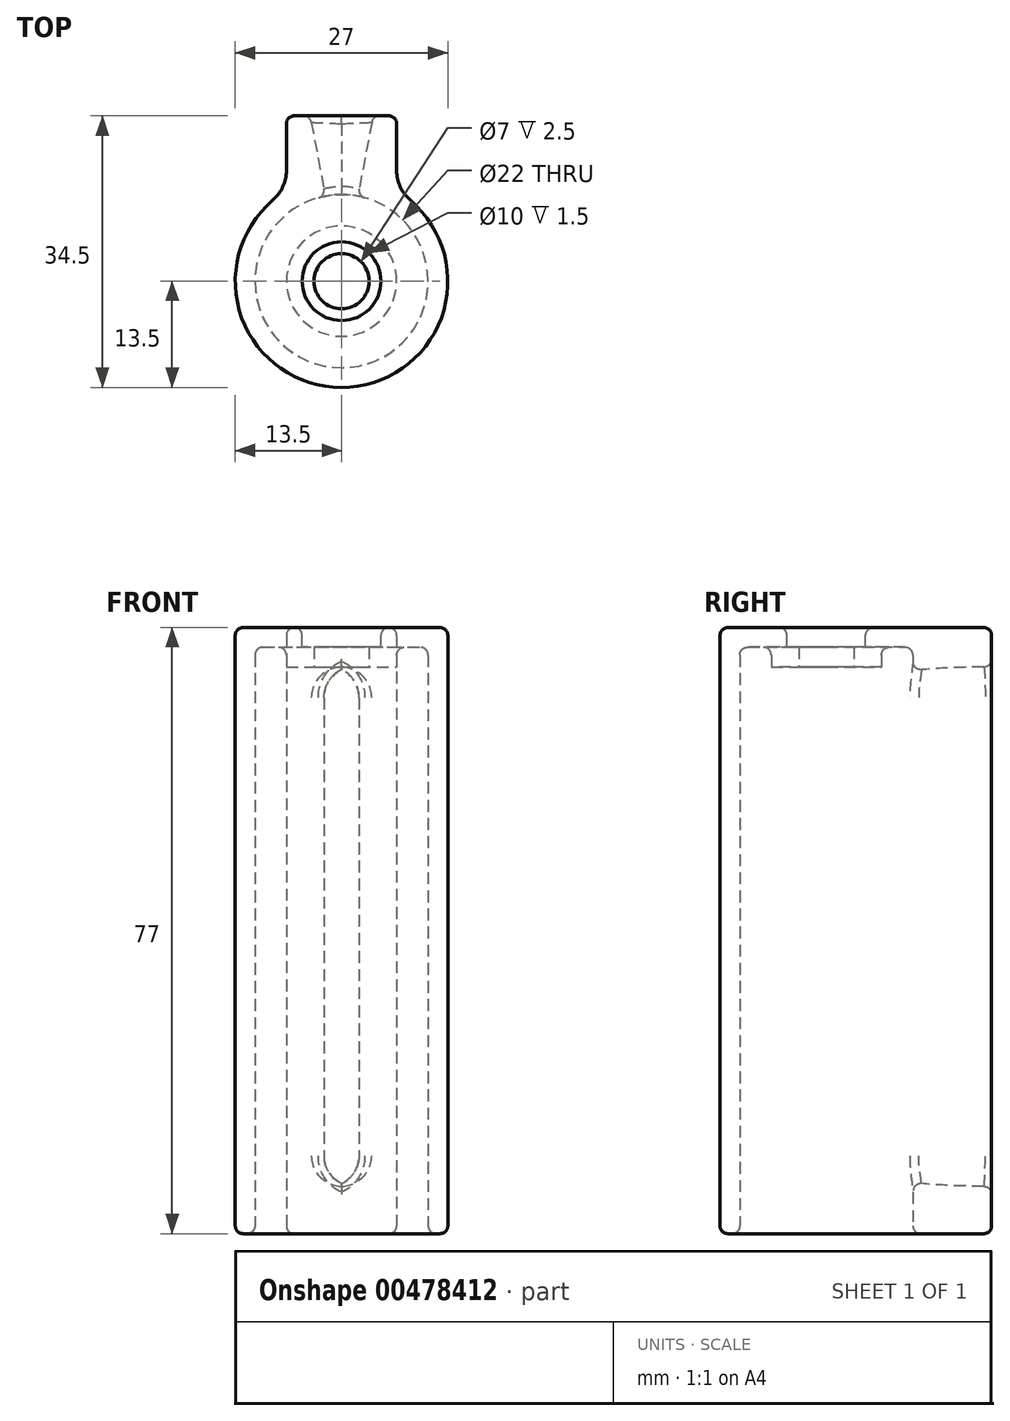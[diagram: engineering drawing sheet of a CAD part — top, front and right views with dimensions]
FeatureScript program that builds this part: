
annotation { "Feature Type Name" : "Feature", "Feature Type Description" : "" }
export const myFeature = defineFeature(function(context is Context, id is Id, definition is map)
    precondition{}
    {
        {
            var Q0;
            Q0=qCreatedBy(makeId("Top.planeOp"),FACE);
            var sketch = newSketch(context, id + "F0", { "sketchPlane" : qUnion([Q0])});
            skArc(sketch, "E0", {"start": v(-8.76, 10.27) * mm, "mid": v(0, -13.5) * mm, "end": v(8.76, 10.27) * mm});
            skCircle(sketch, "E1", {"center": v(0, 0) * mm, "radius": 3.5 * mm});
            skLineSegment(sketch, "E2", {"start": v(0, 0) * mm, "end": v(0, 21) * mm, "construction": true});
            skPoint(sketch, "E3.visualSharp", {"position": v(-7, 11.54) * mm});
            skArc(sketch, "E3.filletArc", {"start": v(-8.76, 10.27) * mm, "mid": v(-7.46, 11.98) * mm, "end": v(-7, 14.08) * mm});
            skPoint(sketch, "E4.visualSharp", {"position": v(7, 11.54) * mm});
            skArc(sketch, "E4.filletArc", {"start": v(7, 14.08) * mm, "mid": v(7.46, 11.98) * mm, "end": v(8.76, 10.27) * mm});
            skPoint(sketch, "E5.visualSharp", {"position": v(7, 21) * mm});
            skPoint(sketch, "E6.visualSharp", {"position": v(-7, 21) * mm});
            skLineSegment(sketch, "E7", {"start": v(-7, 14.08) * mm, "end": v(-7, 20) * mm});
            skLineSegment(sketch, "E8", {"start": v(-6, 21) * mm, "end": v(6, 21) * mm});
            skLineSegment(sketch, "E9", {"start": v(7, 20) * mm, "end": v(7, 14.08) * mm});
            skArc(sketch, "E10.filletArc", {"start": v(-6, 21) * mm, "mid": v(-6.7, 20.7) * mm, "end": v(-7, 20) * mm});
            skArc(sketch, "E11.filletArc", {"start": v(7, 20) * mm, "mid": v(6.7, 20.7) * mm, "end": v(6, 21) * mm});
            skSolve(sketch);
        }
        {
            var Q0;
            Q0 = qSketchRegion(id + "F0", true);
            extrude(context, id + "F1", {"entities" : qUnion([Q0]), "depth" : 77 * mm});
        }
        {
            var Q0;
            Q0=makeQuery(id+"F1.opExtrude","CAP_FACE",FACE,{"disambiguationData":[OSD([sQuery(id+"F0.wireOp",EDGE,"E0")])],"isStart":true});
            var sketch = newSketch(context, id + "F2", { "sketchPlane" : qUnion([Q0])});
            skCircle(sketch, "E12", {"center": v(0, 0) * mm, "radius": 11 * mm});
            skSolve(sketch);
        }
        {
            var Q0;
            Q0 = qSketchRegion(id + "F2", true);
            extrude(context, id + "F3", {"entities" : qUnion([Q0]), "operationType" : NewBodyOperationType.REMOVE, "oppositeDirection" : true, "depth" : 72 * mm});
        }
        {
            var Q0;
            Q0=makeQuery(id+"F3.boolean.opBoolean","COPY",FACE,{"derivedFrom":makeQuery(id+"F3.opExtrude","CAP_FACE",FACE,{"disambiguationData":[OSD([sQuery(id+"F2.wireOp",EDGE,"E12")])],"isStart":false})});
            var sketch = newSketch(context, id + "F4", { "sketchPlane" : qUnion([Q0])});
            skCircle(sketch, "E13", {"center": v(0, 0) * mm, "radius": 11 * mm});
            skCircle(sketch, "E14", {"center": v(0, 0) * mm, "radius": 7 * mm});
            skSolve(sketch);
        }
        {
            var Q0;
            Q0 = qSketchRegion(id + "F4", true);
            extrude(context, id + "F5", {"entities" : qUnion([Q0]), "operationType" : NewBodyOperationType.REMOVE, "oppositeDirection" : true, "depth" : 2.5 * mm});
        }
        {
            var Q0;
            Q0=qCreatedBy(makeId("Top.planeOp"),FACE);
            cPlane(context, id + "F6", {"entities" : qUnion([Q0]), "cplaneType" : CPlaneType.OFFSET, "offset" : 6 * mm, "width" : 150 * mm, "height" : 150 * mm});
        }
        {
            var Q0;
            Q0=qCreatedBy(id+"F6.planeOp",FACE);
            var sketch = newSketch(context, id + "F7", { "sketchPlane" : qUnion([Q0])});
            skLineSegment(sketch, "E15.0", {"start": v(-5, 21) * mm, "end": v(5, 21) * mm, "construction": true});
            skLineSegment(sketch, "E16", {"start": v(0, 21) * mm, "end": v(-4, 21) * mm});
            skLineSegment(sketch, "E17", {"start": v(-4, 21) * mm, "end": v(0, 0) * mm});
            skLineSegment(sketch, "E18", {"start": v(0, 21) * mm, "end": v(4, 21) * mm});
            skLineSegment(sketch, "E19", {"start": v(4, 21) * mm, "end": v(0, 0) * mm});
            skSolve(sketch);
        }
        {
            var Q0;
            Q0 = qSketchRegion(id + "F7", true);
            extrude(context, id + "F8", {"entities" : qUnion([Q0]), "operationType" : NewBodyOperationType.REMOVE, "oppositeDirection" : true, "depth" : -66 * mm});
        }
        {
            var Q0;
            Q0=makeQuery(id+"F1.opExtrude","CAP_FACE",FACE,{"disambiguationData":[OSD([sQuery(id+"F0.wireOp",EDGE,"E0"),sQuery(id+"F0.wireOp",EDGE,"E1"),sQuery(id+"F0.wireOp",EDGE,"E3.filletArc"),sQuery(id+"F0.wireOp",EDGE,"E4.filletArc"),sQuery(id+"F0.wireOp",EDGE,"E7"),sQuery(id+"F0.wireOp",EDGE,"E8"),sQuery(id+"F0.wireOp",EDGE,"E9"),sQuery(id+"F0.wireOp",EDGE,"E10.filletArc"),sQuery(id+"F0.wireOp",EDGE,"E11.filletArc")])],"isStart":false});
            var sketch = newSketch(context, id + "F9", { "sketchPlane" : qUnion([Q0])});
            skCircle(sketch, "E20", {"center": v(0, 0) * mm, "radius": 5 * mm});
            skSolve(sketch);
        }
        {
            var Q0;
            Q0 = qSketchRegion(id + "F9", true);
            extrude(context, id + "F10", {"entities" : qUnion([Q0]), "operationType" : NewBodyOperationType.REMOVE, "oppositeDirection" : true, "depth" : 2.5 * mm});
        }
        {
            var Q0;
            Q0=makeQuery(id+"F8.boolean.opBoolean","COPY",EDGE,{"derivedFrom":makeQuery(id+"F8.opExtrude","CAP_EDGE",EDGE,{"disambiguationData":[OSD([sQuery(id+"F7.wireOp",EDGE,"E17")])],"isStart":false})});
            var Q1;
            Q1=makeQuery(id+"F8.boolean.opBoolean","COPY",EDGE,{"derivedFrom":makeQuery(id+"F8.opExtrude","CAP_EDGE",EDGE,{"disambiguationData":[OSD([sQuery(id+"F7.wireOp",EDGE,"E19")])],"isStart":false})});
            var Q2;
            Q2=makeQuery(id+"F8.boolean.opBoolean","COPY",EDGE,{"derivedFrom":makeQuery(id+"F8.opExtrude","CAP_EDGE",EDGE,{"disambiguationData":[OSD([sQuery(id+"F7.wireOp",EDGE,"E19")])],"isStart":true})});
            var Q3;
            Q3=makeQuery(id+"F8.boolean.opBoolean","COPY",EDGE,{"derivedFrom":makeQuery(id+"F8.opExtrude","CAP_EDGE",EDGE,{"disambiguationData":[OSD([sQuery(id+"F7.wireOp",EDGE,"E17")])],"isStart":true})});
            fillet(context, id + "F11", {"entities" : qUnion([Q0, Q1, Q2, Q3]), "radius" : 3.9 * mm, "tangentPropagation" : true, "allowEdgeOverflow" : false});
        }
        {
            var Q0;
            Q0=makeQuery(id+"F1.opExtrude","CAP_FACE",FACE,{"disambiguationData":[OSD([sQuery(id+"F0.wireOp",EDGE,"E0"),sQuery(id+"F0.wireOp",EDGE,"E1"),sQuery(id+"F0.wireOp",EDGE,"E3.filletArc"),sQuery(id+"F0.wireOp",EDGE,"E4.filletArc"),sQuery(id+"F0.wireOp",EDGE,"E7"),sQuery(id+"F0.wireOp",EDGE,"E8"),sQuery(id+"F0.wireOp",EDGE,"E9"),sQuery(id+"F0.wireOp",EDGE,"E10.filletArc"),sQuery(id+"F0.wireOp",EDGE,"E11.filletArc")])],"isStart":false});
            var Q1;
            Q1=makeQuery(id+"F1.opExtrude","CAP_FACE",FACE,{"disambiguationData":[OSD([sQuery(id+"F0.wireOp",EDGE,"E0"),sQuery(id+"F0.wireOp",EDGE,"E1"),sQuery(id+"F0.wireOp",EDGE,"E3.filletArc"),sQuery(id+"F0.wireOp",EDGE,"E4.filletArc"),sQuery(id+"F0.wireOp",EDGE,"E7"),sQuery(id+"F0.wireOp",EDGE,"E8"),sQuery(id+"F0.wireOp",EDGE,"E9"),sQuery(id+"F0.wireOp",EDGE,"E10.filletArc"),sQuery(id+"F0.wireOp",EDGE,"E11.filletArc")])],"isStart":true});
            var Q2;
            Q2=makeQuery(id+"F1.opExtrude","SWEPT_FACE",FACE,{"disambiguationData":[OSD([sQuery(id+"F0.wireOp",EDGE,"E8")])]});
            var Q3;
            Q3=makeQuery(id+"F8.boolean.opBoolean","INTERSECT",EDGE,{"derivedFrom":[makeQuery(id+"F5.boolean.opBoolean","MERGE",FACE,{"derivedFrom":[makeQuery(id+"F3.boolean.opBoolean","COPY",FACE,{"derivedFrom":makeQuery(id+"F3.opExtrude","SWEPT_FACE",FACE,{"disambiguationData":[OSD([sQuery(id+"F2.wireOp",EDGE,"E12")])]})}),makeQuery(id+"F5.opExtrude","SWEPT_FACE",FACE,{"disambiguationData":[OSD([sQuery(id+"F4.wireOp",EDGE,"E13")])]})]}),makeQuery(id+"F8.opExtrude","SWEPT_FACE",FACE,{"disambiguationData":[OSD([sQuery(id+"F7.wireOp",EDGE,"E19")])]})]});
            var Q4;
            Q4=makeQuery(id+"F5.boolean.opBoolean","COPY",EDGE,{"derivedFrom":makeQuery(id+"F5.opExtrude","CAP_EDGE",EDGE,{"disambiguationData":[OSD([sQuery(id+"F4.wireOp",EDGE,"E14")])],"isStart":true})});
            var Q5;
            Q5=makeQuery(id+"F5.boolean.opBoolean","COPY",EDGE,{"derivedFrom":makeQuery(id+"F5.opExtrude","CAP_EDGE",EDGE,{"disambiguationData":[OSD([sQuery(id+"F4.wireOp",EDGE,"E13")])],"isStart":false})});
            var Q6;
            Q6=makeQuery(id+"F5.boolean.opBoolean","COPY",EDGE,{"derivedFrom":makeQuery(id+"F5.opExtrude","CAP_EDGE",EDGE,{"disambiguationData":[OSD([sQuery(id+"F4.wireOp",EDGE,"E14")])],"isStart":false})});
            var Q7;
            Q7=makeQuery(id+"F8.boolean.opBoolean","INTERSECT",EDGE,{"derivedFrom":[makeQuery(id+"F5.boolean.opBoolean","MERGE",FACE,{"derivedFrom":[makeQuery(id+"F3.boolean.opBoolean","COPY",FACE,{"derivedFrom":makeQuery(id+"F3.opExtrude","SWEPT_FACE",FACE,{"disambiguationData":[OSD([sQuery(id+"F2.wireOp",EDGE,"E12")])]})}),makeQuery(id+"F5.opExtrude","SWEPT_FACE",FACE,{"disambiguationData":[OSD([sQuery(id+"F4.wireOp",EDGE,"E13")])]})]}),makeQuery(id+"F8.opExtrude","CAP_FACE",FACE,{"disambiguationData":[OSD([sQuery(id+"F7.wireOp",EDGE,"E16"),sQuery(id+"F7.wireOp",EDGE,"E17"),sQuery(id+"F7.wireOp",EDGE,"E18"),sQuery(id+"F7.wireOp",EDGE,"E19")])],"isStart":false})]});
            var Q8;
            Q8=makeQuery(id+"F8.boolean.opBoolean","INTERSECT",EDGE,{"derivedFrom":[makeQuery(id+"F5.boolean.opBoolean","MERGE",FACE,{"derivedFrom":[makeQuery(id+"F3.boolean.opBoolean","COPY",FACE,{"derivedFrom":makeQuery(id+"F3.opExtrude","SWEPT_FACE",FACE,{"disambiguationData":[OSD([sQuery(id+"F2.wireOp",EDGE,"E12")])]})}),makeQuery(id+"F5.opExtrude","SWEPT_FACE",FACE,{"disambiguationData":[OSD([sQuery(id+"F4.wireOp",EDGE,"E13")])]})]}),makeQuery(id+"F8.opExtrude","CAP_FACE",FACE,{"disambiguationData":[OSD([sQuery(id+"F7.wireOp",EDGE,"E16"),sQuery(id+"F7.wireOp",EDGE,"E17"),sQuery(id+"F7.wireOp",EDGE,"E18"),sQuery(id+"F7.wireOp",EDGE,"E19")])],"isStart":true})]});
            var Q9;
            Q9=makeQuery(id+"F8.boolean.opBoolean","INTERSECT",EDGE,{"derivedFrom":[makeQuery(id+"F5.boolean.opBoolean","MERGE",FACE,{"derivedFrom":[makeQuery(id+"F3.boolean.opBoolean","COPY",FACE,{"derivedFrom":makeQuery(id+"F3.opExtrude","SWEPT_FACE",FACE,{"disambiguationData":[OSD([sQuery(id+"F2.wireOp",EDGE,"E12")])]})}),makeQuery(id+"F5.opExtrude","SWEPT_FACE",FACE,{"disambiguationData":[OSD([sQuery(id+"F4.wireOp",EDGE,"E13")])]})]}),makeQuery(id+"F8.opExtrude","SWEPT_FACE",FACE,{"disambiguationData":[OSD([sQuery(id+"F7.wireOp",EDGE,"E17")])]})]});
            fillet(context, id + "F12", {"entities" : qUnion([Q0, Q1, Q2, Q3, Q4, Q5, Q6, Q7, Q8, Q9]), "radius" : 1 * mm, "tangentPropagation" : true, "allowEdgeOverflow" : false});
        }
    });
